# Revit family: KingswayGroup_PllHndls_ClassicGripAnti-LigatureCabinetHandle
name_source: partatom
category: Specialty Equipment
units: mm (PartAtom-declared; Revit-internal decimal feet)

## family parameters
Always vertical = Yes
Cut with Voids When Loaded = No
Part Type = Normal
Room Calculation Point = No
Round Connector Dimension = Use Diameter
Shared = No
Work Plane-Based = No

## types (1)
- KingswayGroup_PllHndls_ClassicGripAnti-LigatureCabinetHandle
    AssetType = Fixed
    BIMObjectName = KingswayGroup_PullHandles_ClassicGripAnti-LigatureCabinetHandle
    Category = Pr_30_36_59_64:Pull handles
    Color = For full range of available finishes and colours, contact Kingsway Group
    Default Elevation = 0 mm  [stored 0 ft]
    Description = Classic Grip Cabinet Pull
    DurationUnit = year
    Features = A micro version of the KG61, the Classic Grip Cabinet Pull Handle is a solid, durable and compact anti-ligature handle solution for cabinets and wardrobes within service user areas. Designed to reduce risk, the bolt-fixed cabinet handle offers excellent grip and infection control and is secured using two countersunk security bolts.
    Finish = For full range of available finishes and colours, contact Kingsway Group
    IfcExportAs = IfcDiscreteAccessoryType
    IfcExportType = USERDEFINED
    Manufacturer = Kingsway Group
    ManufacturerName = Kingsway Group
    ManufacturerURL = https://kingswaygroupglobal.com
    Material = For full range of available material, contact Kingsway Group
    Model = KG62
    ModelNumber = KG62
    ModelReference = Classic Grip Anti-Ligature Cabinet Handle
    Name = PullHandles_ClassicGripAnti-LigatureCabinetHandle_KG62_KingswayGroup
    NominalHeight = 100 mm  [stored 0.328084 ft]
    NominalLength = 19 mm  [stored 0.062336 ft]
    NominalWidth = 23 mm  [stored 0.0754593 ft]
    ProductInformation = https://kingswaygroupglobal.com
    Size = 19 x 100 x 23 mm
    URL = https://kingswaygroupglobal.com
    Uniclass2015Code = Pr_30_36_59_64
    Uniclass2015Title = Pull handles
    Uniclass2015Version = Products v1.36
    Version = 1
    WarrantyDescription = 5-Year Guarantee *For faulty manufacture and not for damage
    WarrantyDurationParts = 5
    WarrantyDurationUnit = year

note: [stored X ft] marks values corroborated as IEEE doubles in the binary element streams (Revit-internal decimal feet)

## geometry (parser evidence)
native form markers: Sweep x3
no freeform markers — native parametric forms only
